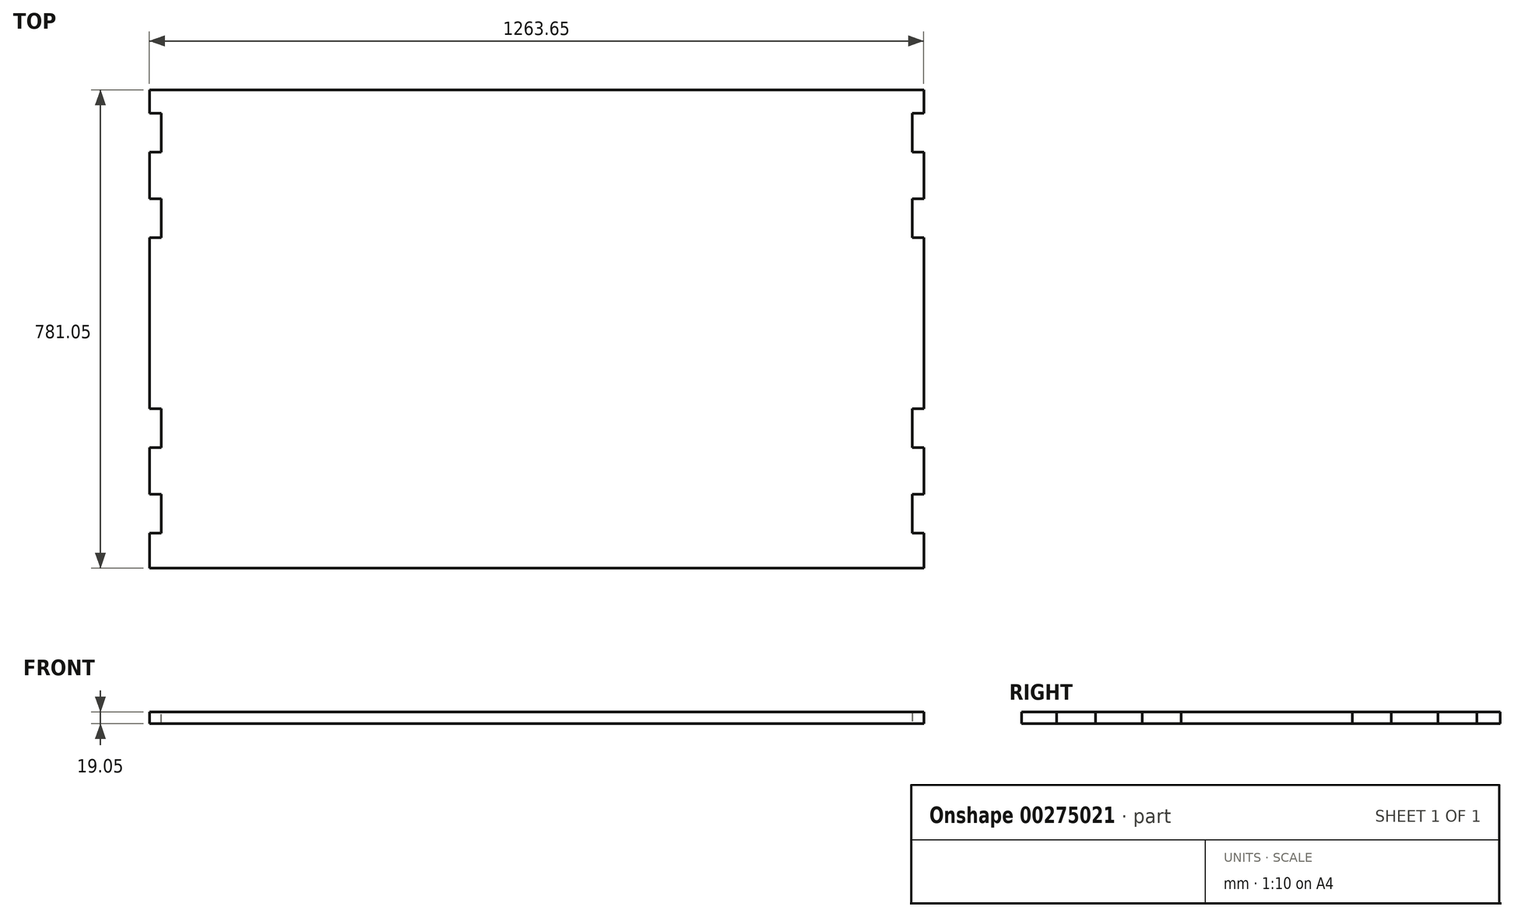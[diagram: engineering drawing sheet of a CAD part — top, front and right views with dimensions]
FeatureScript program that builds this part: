
annotation { "Feature Type Name" : "Feature", "Feature Type Description" : "" }
export const myFeature = defineFeature(function(context is Context, id is Id, definition is map)
    precondition{}
    {
        {
            var Q0;
            Q0=qCreatedBy(makeId("Top.planeOp"),FACE);
            var sketch = newSketch(context, id + "F0", { "sketchPlane" : qUnion([Q0])});
            skLineSegment(sketch, "E0.bottom", {"start": v(-454.8, 377.48) * mm, "end": v(808.84, 377.48) * mm});
            skLineSegment(sketch, "E0.top", {"start": v(-454.8, -403.57) * mm, "end": v(808.84, -403.57) * mm});
            skLineSegment(sketch, "E0.left", {"start": v(-454.8, 377.48) * mm, "end": v(-454.8, -403.57) * mm});
            skLineSegment(sketch, "E0.right", {"start": v(808.84, 377.48) * mm, "end": v(808.84, -403.57) * mm});
            skSolve(sketch);
        }
        {
            var Q0;
            Q0 = qSketchRegion(id + "F0", true);
            extrude(context, id + "F1", {"entities" : qUnion([Q0]), "offsetDistance" : 25.4 * mm, "depth" : 19.05 * mm});
        }
        {
            var Q0;
            Q0=makeQuery(id+"F1.opExtrude","SWEPT_FACE",FACE,{"disambiguationData":[OSD([sQuery(id+"F0.wireOp",EDGE,"E0.right")])]});
            var sketch = newSketch(context, id + "F2", { "sketchPlane" : qUnion([Q0])});
            skLineSegment(sketch, "E1", {"start": v(377.48, 19.05) * mm, "end": v(-403.57, 19.05) * mm});
            skLineSegment(sketch, "E2.bottom", {"start": v(-346.42, 19.05) * mm, "end": v(-282.92, 19.05) * mm});
            skLineSegment(sketch, "E2.top", {"start": v(-346.42, 0) * mm, "end": v(-282.92, 0) * mm});
            skLineSegment(sketch, "E2.left", {"start": v(-346.42, 19.05) * mm, "end": v(-346.42, 0) * mm});
            skLineSegment(sketch, "E2.right", {"start": v(-282.92, 19.05) * mm, "end": v(-282.92, 0) * mm});
            skLineSegment(sketch, "E3.bottom", {"start": v(-206.72, 19.05) * mm, "end": v(-143.22, 19.05) * mm});
            skLineSegment(sketch, "E3.top", {"start": v(-206.72, 0) * mm, "end": v(-143.22, 0) * mm});
            skLineSegment(sketch, "E3.left", {"start": v(-206.72, 19.05) * mm, "end": v(-206.72, 0) * mm});
            skLineSegment(sketch, "E3.right", {"start": v(-143.22, 19.05) * mm, "end": v(-143.22, 0) * mm});
            skLineSegment(sketch, "E4.bottom", {"start": v(339.38, 19.05) * mm, "end": v(275.88, 19.05) * mm});
            skLineSegment(sketch, "E4.top", {"start": v(339.38, 0) * mm, "end": v(275.88, 0) * mm});
            skLineSegment(sketch, "E4.left", {"start": v(339.38, 19.05) * mm, "end": v(339.38, 0) * mm});
            skLineSegment(sketch, "E4.right", {"start": v(275.88, 19.05) * mm, "end": v(275.88, 0) * mm});
            skLineSegment(sketch, "E5.bottom", {"start": v(199.68, 19.05) * mm, "end": v(136.18, 19.05) * mm});
            skLineSegment(sketch, "E5.top", {"start": v(199.68, 0) * mm, "end": v(136.18, 0) * mm});
            skLineSegment(sketch, "E5.left", {"start": v(199.68, 19.05) * mm, "end": v(199.68, 0) * mm});
            skLineSegment(sketch, "E5.right", {"start": v(136.18, 19.05) * mm, "end": v(136.18, 0) * mm});
            skSolve(sketch);
        }
        {
            var Q0;
            {Q0=qUnion([makeQuery(id+"F2.imprint","IMPRINT",FACE,{"disambiguationData":[TD([[makeQuery(id+"F2.imprint","IMPRINT",EDGE,{"derivedFrom":sQuery(id+"F2.wireOp",EDGE,"E4.top")}),-1.0]])]}),makeQuery(id+"F2.imprint","IMPRINT",FACE,{"disambiguationData":[TD([[makeQuery(id+"F2.imprint","IMPRINT",EDGE,{"derivedFrom":sQuery(id+"F2.wireOp",EDGE,"E5.top")}),-1.0]])]}),makeQuery(id+"F2.imprint","IMPRINT",FACE,{"disambiguationData":[TD([[makeQuery(id+"F2.imprint","IMPRINT",EDGE,{"derivedFrom":sQuery(id+"F2.wireOp",EDGE,"E3.top")}),-1.0]])]}),makeQuery(id+"F2.imprint","IMPRINT",FACE,{"disambiguationData":[TD([[makeQuery(id+"F2.imprint","IMPRINT",EDGE,{"derivedFrom":sQuery(id+"F2.wireOp",EDGE,"E2.top")}),-1.0]])]})]);}
            extrude(context, id + "F3", {"entities" : qUnion([Q0]), "operationType" : NewBodyOperationType.REMOVE, "oppositeDirection" : true, "depth" : 19.05 * mm, "offsetDistance" : 25.4 * mm});
        }
        {
            var Q0;
            Q0=makeQuery(id+"F1.opExtrude","SWEPT_FACE",FACE,{"disambiguationData":[OSD([sQuery(id+"F0.wireOp",EDGE,"E0.left")])]});
            var sketch = newSketch(context, id + "F4", { "sketchPlane" : qUnion([Q0])});
            skLineSegment(sketch, "E6", {"start": v(-377.48, 0) * mm, "end": v(403.57, 0) * mm});
            skLineSegment(sketch, "E7.bottom", {"start": v(346.42, 0) * mm, "end": v(282.92, 0) * mm});
            skLineSegment(sketch, "E7.top", {"start": v(346.42, 19.05) * mm, "end": v(282.92, 19.05) * mm});
            skLineSegment(sketch, "E7.left", {"start": v(346.42, 0) * mm, "end": v(346.42, 19.05) * mm});
            skLineSegment(sketch, "E7.right", {"start": v(282.92, 0) * mm, "end": v(282.92, 19.05) * mm});
            skLineSegment(sketch, "E8.bottom", {"start": v(206.72, 0) * mm, "end": v(143.22, 0) * mm});
            skLineSegment(sketch, "E8.top", {"start": v(206.72, 19.05) * mm, "end": v(143.22, 19.05) * mm});
            skLineSegment(sketch, "E8.left", {"start": v(206.72, 0) * mm, "end": v(206.72, 19.05) * mm});
            skLineSegment(sketch, "E8.right", {"start": v(143.22, 0) * mm, "end": v(143.22, 19.05) * mm});
            skLineSegment(sketch, "E9.bottom", {"start": v(-339.38, 0) * mm, "end": v(-275.88, 0) * mm});
            skLineSegment(sketch, "E9.top", {"start": v(-339.38, 19.05) * mm, "end": v(-275.88, 19.05) * mm});
            skLineSegment(sketch, "E9.left", {"start": v(-339.38, 0) * mm, "end": v(-339.38, 19.05) * mm});
            skLineSegment(sketch, "E9.right", {"start": v(-275.88, 0) * mm, "end": v(-275.88, 19.05) * mm});
            skLineSegment(sketch, "E10.bottom", {"start": v(-199.68, 0) * mm, "end": v(-136.18, 0) * mm});
            skLineSegment(sketch, "E10.top", {"start": v(-199.68, 19.05) * mm, "end": v(-136.18, 19.05) * mm});
            skLineSegment(sketch, "E10.left", {"start": v(-199.68, 0) * mm, "end": v(-199.68, 19.05) * mm});
            skLineSegment(sketch, "E10.right", {"start": v(-136.18, 0) * mm, "end": v(-136.18, 19.05) * mm});
            skSolve(sketch);
        }
        {
            var Q0;
            {Q0=qUnion([makeQuery(id+"F4.imprint","IMPRINT",FACE,{"disambiguationData":[TD([[makeQuery(id+"F4.imprint","IMPRINT",EDGE,{"derivedFrom":sQuery(id+"F4.wireOp",EDGE,"E10.top")}),-1.0]])]}),makeQuery(id+"F4.imprint","IMPRINT",FACE,{"disambiguationData":[TD([[makeQuery(id+"F4.imprint","IMPRINT",EDGE,{"derivedFrom":sQuery(id+"F4.wireOp",EDGE,"E8.top")}),-1.0]])]}),makeQuery(id+"F4.imprint","IMPRINT",FACE,{"disambiguationData":[TD([[makeQuery(id+"F4.imprint","IMPRINT",EDGE,{"derivedFrom":sQuery(id+"F4.wireOp",EDGE,"E7.top")}),-1.0]])]}),makeQuery(id+"F4.imprint","IMPRINT",FACE,{"disambiguationData":[TD([[makeQuery(id+"F4.imprint","IMPRINT",EDGE,{"derivedFrom":sQuery(id+"F4.wireOp",EDGE,"E9.top")}),-1.0]])]})]);}
            extrude(context, id + "F5", {"entities" : qUnion([Q0]), "operationType" : NewBodyOperationType.REMOVE, "oppositeDirection" : true, "depth" : 19.05 * mm, "offsetDistance" : 25.4 * mm});
        }
    });
